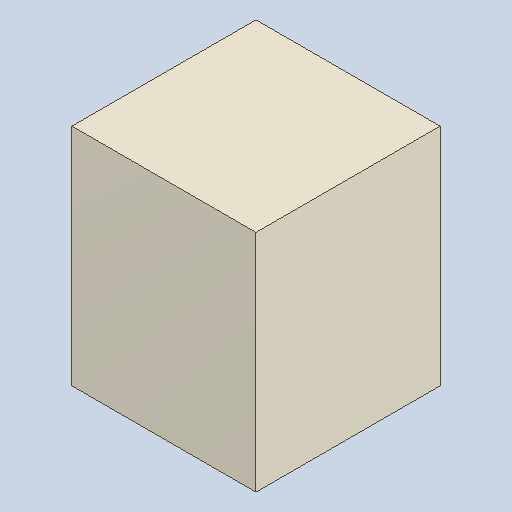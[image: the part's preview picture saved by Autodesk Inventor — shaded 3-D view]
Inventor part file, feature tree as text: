
AUTODESK INVENTOR PART (.ipt)
format: ipt  version: 2023.4 (Build 274418000, 418)  size: 82,944 bytes
history: native  units: mm
features: extrude x1
ambient origin geometry x8: Origin, YZ Plane, XZ Plane, XY Plane, X Axis, Y Axis, Z Axis, Center Point
bodies: Solid1 (feature_tree)
feature tree (1):
  extrude  "Extruded_4"  [1 undecoded]
note: 1 required parameter value undecoded (feature->parameter linkage not recoverable at this tier; creation-order binding heuristic only, values carry confidence <= 0.55)
